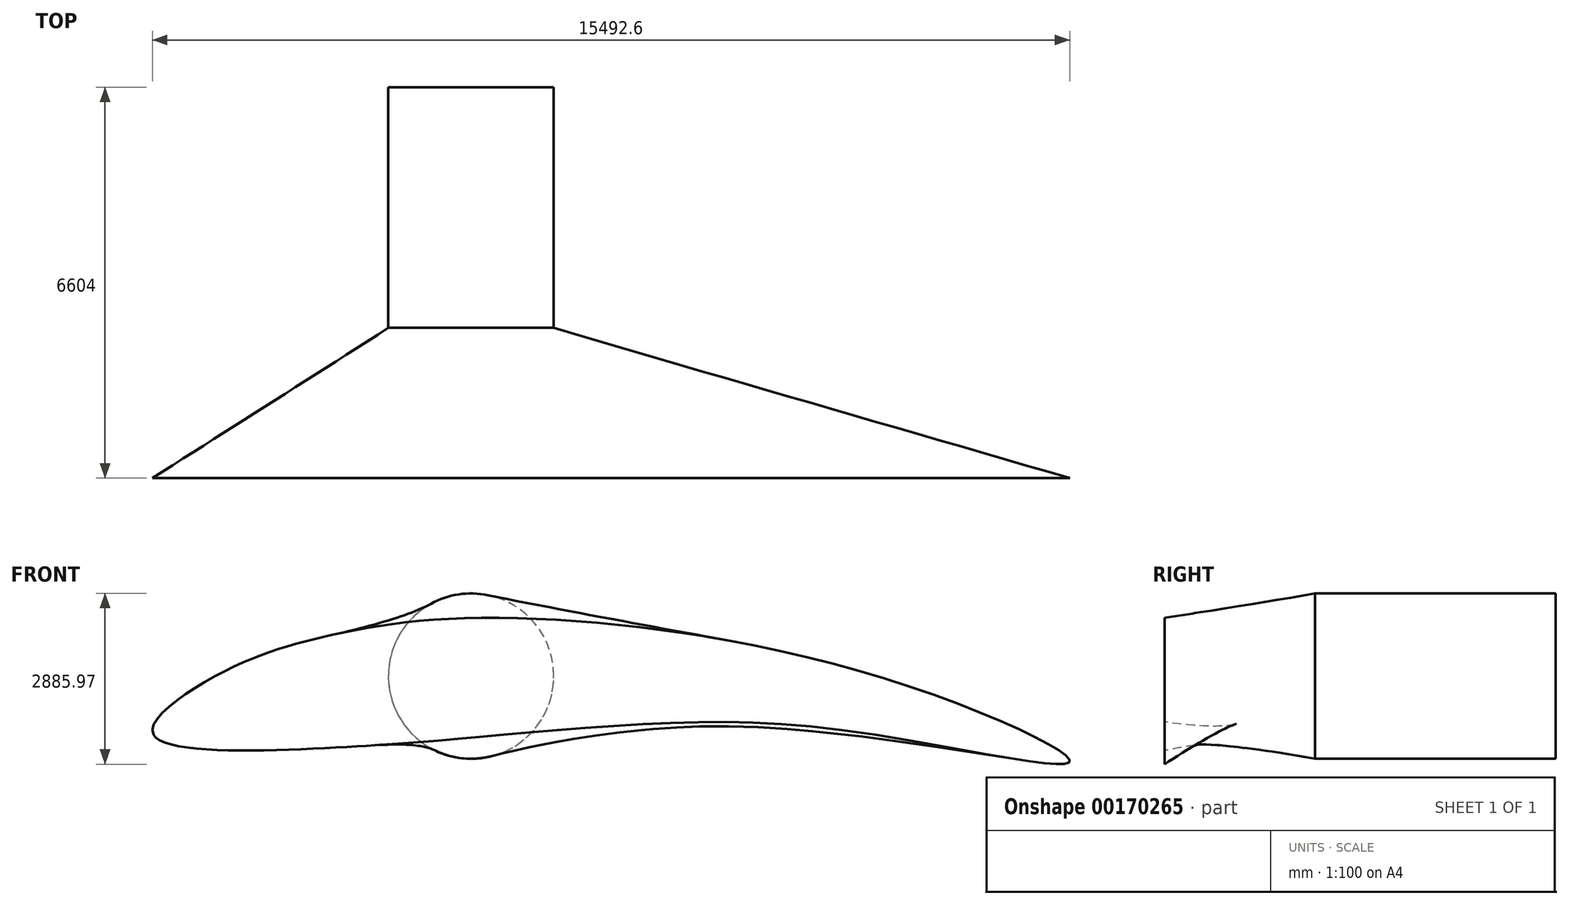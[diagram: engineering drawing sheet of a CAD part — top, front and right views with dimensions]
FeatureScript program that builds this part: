
annotation { "Feature Type Name" : "Feature", "Feature Type Description" : "" }
export const myFeature = defineFeature(function(context is Context, id is Id, definition is map)
    precondition{}
    {
        {
            var Q0;
            Q0=qCreatedBy(makeId("Front.planeOp"),FACE);
            var sketch = newSketch(context, id + "F0", { "sketchPlane" : qUnion([Q0])});
            skCircle(sketch, "E0", {"center": v(0, 0) * mm, "radius": 1397 * mm});
            skSolve(sketch);
        }
        {
            var Q0;
            Q0 = qSketchRegion(id + "F0", true);
            extrude(context, id + "F1", {"entities" : qUnion([Q0]), "depth" : 4064 * mm});
        }
        {
            var Q0;
            Q0=makeQuery(id+"F1.opExtrude","CAP_FACE",FACE,{"disambiguationData":[OSD([sQuery(id+"F0.wireOp",EDGE,"E0")])],"isStart":false});
            cPlane(context, id + "F2", {"entities" : qUnion([Q0]), "cplaneType" : CPlaneType.OFFSET, "offset" : 2540 * mm, "width" : 152.4 * mm, "height" : 152.4 * mm});
        }
        {
            var Q0;
            Q0=qCreatedBy(id+"F2.planeOp",FACE);
            var sketch = newSketch(context, id + "F3", { "sketchPlane" : qUnion([Q0])});
            skFitSpline(sketch, "E1", {"points": [v(-5365.42, -987.26) * mm, v(-4318.96, 0) * mm, v(-2568.56, 642.54) * mm, v(0, 981.7) * mm, v(6855.36, 0) * mm, v(10103.24, -1454) * mm, v(6872.99, -997.27) * mm, v(3169.68, -798.85) * mm, v(0, -1041.1) * mm, v(-2090.63, -1196.83) * mm, v(-5365.42, -987.26) * mm]});
            skSolve(sketch);
        }
        {
            var Q0;
            Q0=makeQuery(id+"F3.imprint","IMPRINT",FACE,{"disambiguationData":[TD([[makeQuery(id+"F3.imprint","IMPRINT",EDGE,{"derivedFrom":sQuery(id+"F3.wireOp",EDGE,"E1")}),-1.0]])]});
            var Q1;
            Q1=makeQuery(id+"F1.opExtrude","CAP_FACE",FACE,{"disambiguationData":[OSD([sQuery(id+"F0.wireOp",EDGE,"E0")])],"isStart":false});
            loft(context, id + "F4", {"sheetProfilesArray" : [{ "sheetProfileEntities" : qUnion([Q0]) }, { "sheetProfileEntities" : qUnion([Q1]) }]});
        }
    });
